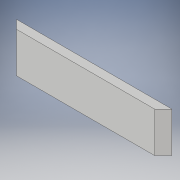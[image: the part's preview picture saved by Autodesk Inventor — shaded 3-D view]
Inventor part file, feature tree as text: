
AUTODESK INVENTOR PART (.ipt)
format: ipt  version: 2019 (Build 230136000, 136)  size: 92,672 bytes
history: native  units: in
note: dims shown in document units (in); Inventor stores cm internally (conversion verified against a paired STEP export)
features: extrude x1, chamfer x1, sketch x1
ambient origin geometry x8: Origin, YZ Plane, XZ Plane, XY Plane, X Axis, Y Axis, Z Axis, Center Point
bodies: Solid1 (feature_tree)
feature tree (3):
  extrude  "Extrusion1"  Depth=0.75in
  chamfer  "Chamfer1"  Distance=3.5in
  sketch  "Sketch1"  dims[d0=13.5in d1=0.75in d2=3.5in d3=0.0in d4=0.75in d5=0.125in d6=45.0deg]
